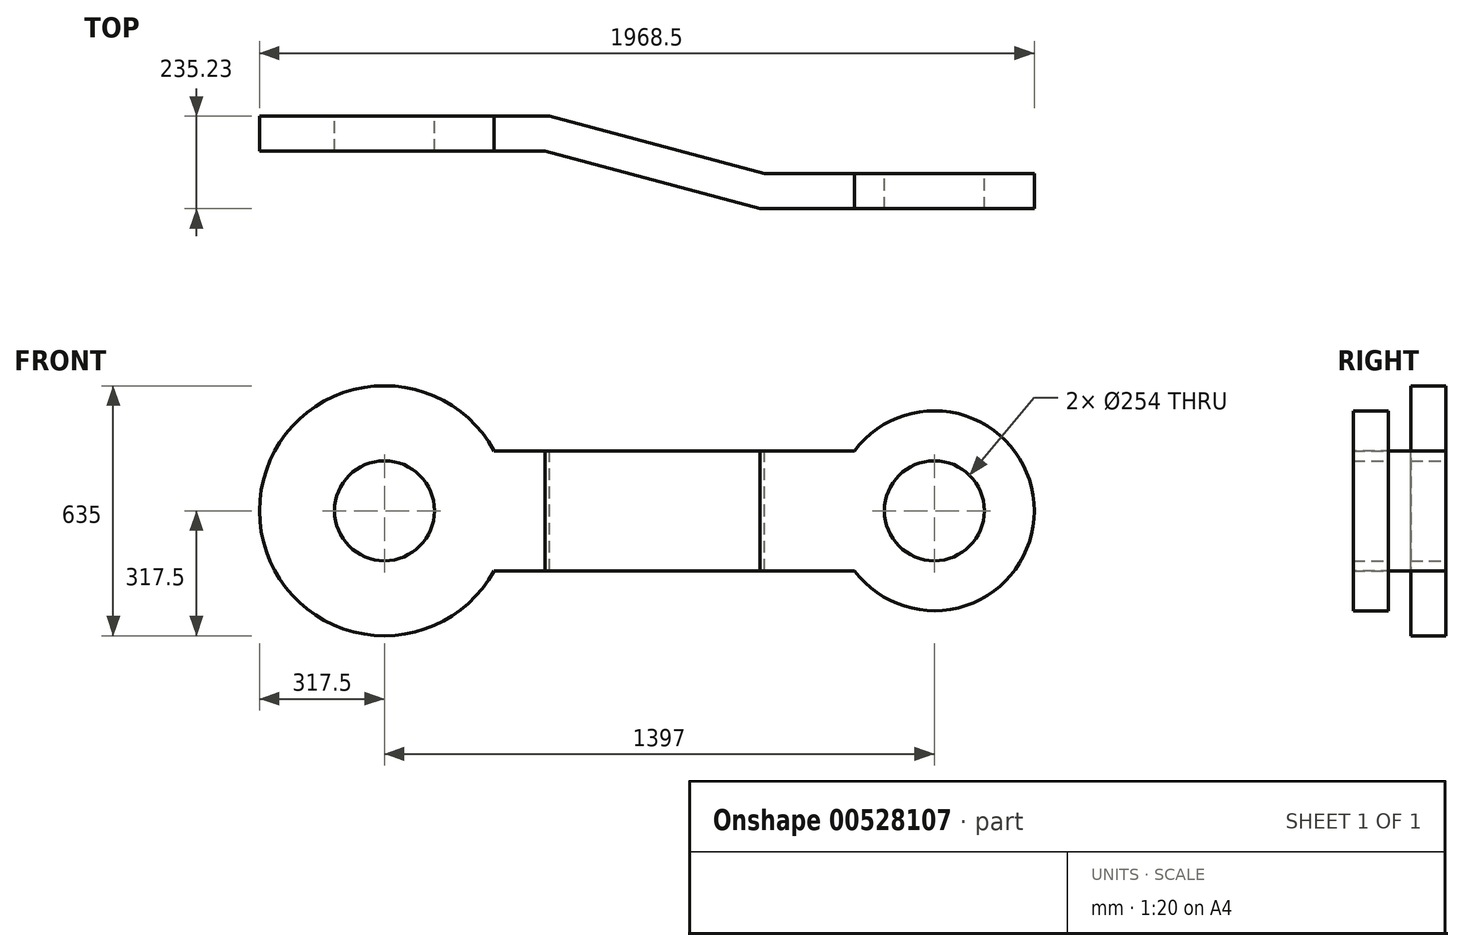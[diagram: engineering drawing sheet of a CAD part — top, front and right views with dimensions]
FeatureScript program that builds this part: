
annotation { "Feature Type Name" : "Feature", "Feature Type Description" : "" }
export const myFeature = defineFeature(function(context is Context, id is Id, definition is map)
    precondition{}
    {
        {
            var Q0;
            Q0=qCreatedBy(makeId("Front.planeOp"),FACE);
            var sketch = newSketch(context, id + "F0", { "sketchPlane" : qUnion([Q0])});
            skCircle(sketch, "E0", {"center": v(0, 0) * mm, "radius": 317.5 * mm});
            skCircle(sketch, "E1", {"center": v(1397, 0) * mm, "radius": 254 * mm});
            skLineSegment(sketch, "E2", {"start": v(0, 0) * mm, "end": v(1397, 0) * mm, "construction": true});
            skLineSegment(sketch, "E3", {"start": v(278.53, 152.4) * mm, "end": v(1193.8, 152.4) * mm});
            skLineSegment(sketch, "E4.MirrorCS", {"start": v(278.53, -152.4) * mm, "end": v(1193.8, -152.4) * mm});
            skCircle(sketch, "E5", {"center": v(0, 0) * mm, "radius": 127 * mm});
            skCircle(sketch, "E6", {"center": v(1397, 0) * mm, "radius": 127 * mm});
            skSolve(sketch);
        }
        {
            var Q0;
            Q0 = qSketchRegion(id + "F0", true);
            extrude(context, id + "F1", {"entities" : qUnion([Q0]), "depth" : 660.4 * mm, "offsetDistance" : 25.4 * mm});
        }
        {
            var Q0;
            Q0=qCreatedBy(makeId("Top.planeOp"),FACE);
            var sketch = newSketch(context, id + "F2", { "sketchPlane" : qUnion([Q0])});
            skLineSegment(sketch, "E7", {"start": v(-317.5, -660.4) * mm, "end": v(-317.5, 0) * mm});
            skLineSegment(sketch, "E8", {"start": v(-317.5, 0) * mm, "end": v(419.1, 0) * mm});
            skLineSegment(sketch, "E9", {"start": v(419.1, 0) * mm, "end": v(965.2, -146.33) * mm});
            skLineSegment(sketch, "E10", {"start": v(965.2, -146.33) * mm, "end": v(1651, -146.33) * mm});
            skLineSegment(sketch, "E11", {"start": v(1651, 0) * mm, "end": v(1651, -660.4) * mm});
            skLineSegment(sketch, "E12.0", {"start": v(953.5, -235.23) * mm, "end": v(1651, -235.23) * mm});
            skLineSegment(sketch, "E12.1", {"start": v(407.4, -88.9) * mm, "end": v(953.5, -235.23) * mm});
            skLineSegment(sketch, "E12.2", {"start": v(-317.5, -88.9) * mm, "end": v(407.4, -88.9) * mm});
            skLineSegment(sketch, "E13", {"start": v(1651, -146.33) * mm, "end": v(1651, -235.23) * mm});
            skLineSegment(sketch, "E14", {"start": v(-317.5, 0) * mm, "end": v(-317.5, -88.9) * mm});
            skSolve(sketch);
        }
        {
            var Q0;
            Q0 = qSketchRegion(id + "F2", true);
            extrude(context, id + "F3", {"entities" : qUnion([Q0]), "operationType" : NewBodyOperationType.INTERSECT, "endBound" : BoundingType.SYMMETRIC, "oppositeDirection" : true, "depth" : 980.44 * mm, "offsetDistance" : 25.4 * mm});
        }
    });
